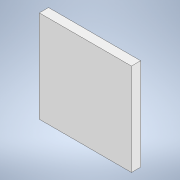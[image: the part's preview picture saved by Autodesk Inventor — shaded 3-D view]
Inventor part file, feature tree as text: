
AUTODESK INVENTOR PART (.ipt)
format: ipt  version: 2022 (Build 260153000, 153)  size: 88,576 bytes
history: native  units: mm
features: extrude x1, sketch x1
ambient origin geometry x8: Origin, YZ Plane, XZ Plane, XY Plane, X Axis, Y Axis, Z Axis, Center Point
bodies: Solid1 (feature_tree)
feature tree (2):
  extrude  "Extrusion1"  Depth=31.75mm
  sketch  "Sketch1"  dims[d0=31.75mm d1=31.75mm d2=3.175mm d3=0.0mm]
